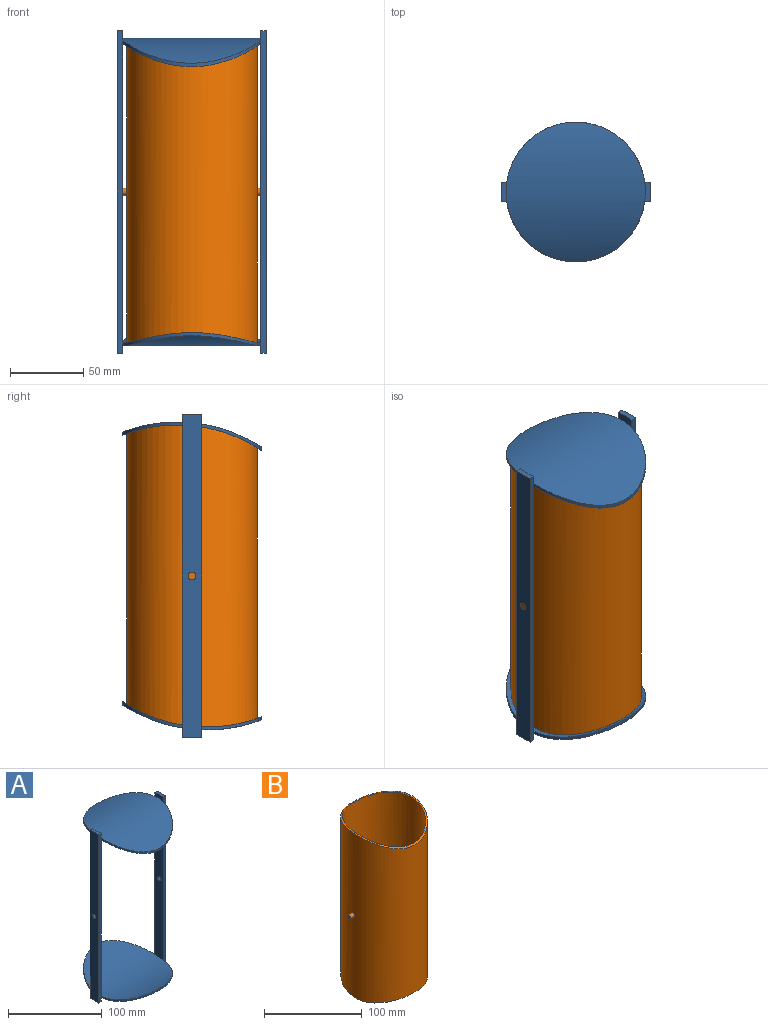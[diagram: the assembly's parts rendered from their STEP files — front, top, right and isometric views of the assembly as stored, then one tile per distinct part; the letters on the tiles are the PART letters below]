
ASSEMBLY  parts=2 mates=1
PART A: 26 faces, bbox 101.7x95x220 mm
  f0: cylinder r=47.5mm len=205.88mm, axis (0,0,-1), area 2658.5mm2, adj f5,f8,f10,f23,f25
  f1: cylinder r=47.5mm len=205.88mm, axis (0,0,-1), area 2658.5mm2, adj f5,f14,f16,f23,f24
  f2: cylinder r=47.5mm len=94.1mm, axis (0,0,-1), area 281.6mm2, adj f4,f5,f10,f16
  f3: cylinder r=47.5mm len=94.1mm, axis (0,0,-1), area 303mm2, adj f4,f5,f8,f14
  f4: cylinder r=105mm len=95.01mm, axis (-1,0,0), area 7327.8mm2, adj f2,f3,f6,f13
  f5: cylinder r=103mm len=95.01mm, axis (-1,0,0), area 7338.1mm2, adj f0,f1,f2,f3
  f6: cylinder r=47.5mm len=13.03mm, axis (0,0,-1), area 72.5mm2, adj f4,f8,f10,f12
  f7: cylinder r=47.5mm len=13.03mm, axis (0,0,-1), area 72.5mm2, adj f8,f10,f11,f21
  f8: plane 220x3.8mm, normal (0,1,0), area 836.1mm2, adj f0,f3,f6,f7,f9,f11,f12,f20
  f9: plane 220x13.03mm, normal (-1,0,0), area 2847mm2, adj f8,f10,f11,f12,f25
  f10: plane 220x3.8mm, normal (0,-1,0), area 836.1mm2, adj f0,f2,f6,f7,f9,f11,f12,f22
  f11: plane 13.03x3.8mm, normal (0,0,1), area 45.6mm2, adj f7,f8,f9,f10
  f12: plane 13.03x3.8mm, normal (0,0,-1), area 45.6mm2, adj f6,f8,f9,f10
  f13: cylinder r=47.5mm len=13.03mm, axis (0,0,-1), area 72.5mm2, adj f4,f14,f16,f19
  f14: plane 220x3.8mm, normal (0,1,0), area 836.1mm2, adj f1,f3,f13,f15,f17,f18,f19,f20
  f15: cylinder r=47.5mm len=13.03mm, axis (0,0,-1), area 72.5mm2, adj f14,f16,f18,f21
  f16: plane 220x3.8mm, normal (0,-1,0), area 836.1mm2, adj f1,f2,f13,f15,f17,f18,f19,f22
  f17: plane 220x13.03mm, normal (1,0,0), area 2847mm2, adj f14,f16,f18,f19,f24
  f18: plane 13.03x3.8mm, normal (0,0,1), area 45.6mm2, adj f14,f15,f16,f17
  f19: plane 13.03x3.8mm, normal (0,0,-1), area 45.6mm2, adj f13,f14,f16,f17
  f20: cylinder r=47.5mm len=94.1mm, axis (0,0,-1), area 281.6mm2, adj f8,f14,f21,f23
  f21: cylinder r=105mm len=95.01mm, axis (-1,0,0), area 7327.8mm2, adj f7,f15,f20,f22
  f22: cylinder r=47.5mm len=94.1mm, axis (0,0,-1), area 303mm2, adj f10,f16,f21,f23
  f23: cylinder r=103mm len=95.01mm, axis (-1,0,0), area 7338.1mm2, adj f0,f1,f20,f22
  f24: cylinder r=2.5mm len=5mm, axis (1,0,0), area 53.2mm2, adj f1,f17
  f25: cylinder r=2.5mm len=5mm, axis (1,0,0), area 53.2mm2, adj f0,f9
PART B: 9 faces, bbox 102x89x206 mm
  f0: cylinder r=42.5mm len=206mm, axis (0,0,-1), area 52250.7mm2, adj f2,f3,f8
  f1: cylinder r=44.5mm len=206mm, axis (0,0,-1), area 54452mm2, adj f2,f3,f5,f7
  f2: cylinder r=103mm len=89mm, axis (-1,0,0), area 578.3mm2, adj f0,f1
  f3: cylinder r=103mm len=89mm, axis (-1,0,0), area 575.9mm2, adj f0,f1
  f4: plane 5x5mm, normal (-1,0,0), area 19.6mm2, adj f5
  f5: cylinder r=2.5mm len=6.57mm, axis (-1,0,0), area 102.7mm2, adj f1,f4
  f6: plane 5x5mm, normal (1,0,0), area 19.6mm2, adj f7
  f7: cylinder r=2.5mm len=6.57mm, axis (-1,0,0), area 102.7mm2, adj f1,f6
  f8: cylinder r=2.5mm len=85mm, axis (-1,0,0), area 1334mm2, adj f0
PLACE A rot(axis=(-1,0,0),0deg) t=(111.56,-98.63,11.56)mm
PLACE B t=(111.71,-98.63,11.56)mm fixed
MATE revolute A.f24 <-> B.f5  axis (-1,0,0) through (60.71,-108.63,11.56)mm
